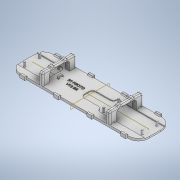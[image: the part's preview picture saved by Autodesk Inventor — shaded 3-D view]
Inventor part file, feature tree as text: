
AUTODESK INVENTOR PART (.ipt)
format: ipt  version: 2021 (Build 250183000, 183)  size: 2,626,048 bytes
history: native  units: in
note: dims shown in document units (in); Inventor stores cm internally (conversion verified against a paired STEP export)
features: sketch x16, extrude x11, fillet x7, mirror x6, revolve x5, plane x2
ambient origin geometry x8: Origin, YZ Plane, XZ Plane, XY Plane, X Axis, Y Axis, Z Axis, Center Point
bodies: Solid1 (feature_tree)
feature tree (47):
  extrude  "Extrusion1"  Depth=4.9606in
  extrude  "Extrusion2"  TaperAngle=0.0deg  [1 undecoded]
  extrude  "Extrusion3"  Depth=0.2362in
  plane  "Work Plane1"
  plane  "Work Plane2"
  extrude  "Extrusion5"  TaperAngle=0.0deg  [1 undecoded]
  fillet  "Fillet2"  [1 undecoded]
  mirror  "Mirror3"
  extrude  "Extrusion6"  TaperAngle=0.0deg  [1 undecoded]
  extrude  "Extrusion7"  TaperAngle=0.0deg  [1 undecoded]
  extrude  "Extrusion9"  TaperAngle=0.0deg  [1 undecoded]
  extrude  "Extrusion10"  Depth=0.2362in
  fillet  "Fillet4"  Radius=1.3386in
  mirror  "Mirror4"
  mirror  "Mirror5"
  fillet  "Fillet5"  [1 undecoded]
  extrude  "Extrusion11"  TaperAngle=0.0deg  [1 undecoded]
  fillet  "Fillet6"  [1 undecoded]
  revolve  "Revolution1"  [1 undecoded]
  revolve  "Revolution2"  [1 undecoded]
  revolve  "Revolution3"  [1 undecoded]
  revolve  "Revolution4"  [1 undecoded]
  extrude  "Extrusion12"  Depth=0.0945in
  revolve  "Revolution5"  [1 undecoded]
  extrude  "Extrusion13"  TaperAngle=0.0deg  [1 undecoded]
  mirror  "Mirror8"
  mirror  "Mirror9"
  mirror  "Mirror10"
  fillet  "Fillet9"  [1 undecoded]
  fillet  "Fillet10"  [1 undecoded]
  fillet  "Fillet11"  Radius=0.7in
  sketch  "Sketch1"  dims[d0=0.1102in d1=0.0in d2=4.9606in]
  sketch  "Sketch2"  dims[d3=1.5512in d4=0.0in]
  sketch  "Sketch3"  dims[d5=0.0in d6=0.2362in]
  sketch  "Sketch6"  dims[d7=0.0787in d8=0.0in d9=0.0in d10=0.0in]
  sketch  "Sketch7"  dims[d11=0.0in d12=0.0in]
  sketch  "Sketch8"  dims[d13=0.0472in d14=0.0in]
  sketch  "Sketch13"  dims[d15=-0.7756in d16=0.0in]
  sketch  "Sketch14"  dims[d17=0.0in d18=0.2362in d19=1.3386in d20=0.0in]
  sketch  "Sketch15"  dims[d21=0.0in d22=0.0in d23=0.0in]
  sketch  "Sketch20"  dims[d24=-2.4803in d28=0.5354in d29=0.0in]
  sketch  "Sketch21"  dims[d30=0.5354in d31=0.9449in]
  sketch  "Sketch22"  dims[d32=2.7559in d33=0.4724in]
  sketch  "Sketch23"  dims[d34=0.7874in d35=0.0394in d36=0.0in]
  sketch  "Sketch25"  dims[d37=0.0945in d38=0.0945in]
  sketch  "Sketch26"  dims[d39=0.0945in d40=0.0945in]
  sketch  "Sketch27"  dims[d41=0.0in d42=0.0in d43=0.0in d44=0.0in d45=0.7in d46=1.8in d47=0.35in d48=0.1811in d49=0.0in d60=1.9685in d61=0.9449in d62=0.4724in d63=1.6929in d64=0.0945in d65=0.0945in d66=0.0945in d67=0.0945in d68=0.0in d69=0.0in d70=0.0in d71=0.0in d72=0.9in d73=0.7in d74=0.35in d75=0.1969in d76=0.5709in d78=0.0in d79=0.4567in d80=0.0in d81=0.0in d82=0.0in d83=0.0in d84=0.0in d85=0.0787in d86=0.0in d88=0.0787in d89=0.1575in d90=0.7874in d91=0.3937in d92=0.0394in d93=0.0in d96=0.9843in d97=0.5512in d98=0.2756in d99=0.1969in d111=90.0deg d112=90.0deg d113=90.0deg d114=90.0deg d116=0.2362in d117=0.0in d118=0.0in d119=0.1181in d120=0.0394in d121=0.0in d122=0.0787in d123=0.0394in d124=180.0deg d125=0.0787in d126=0.1181in d127=0.0157in d128=0.0in d131=0.0394in d132=0.0472in d133=0.0551in]
note: 17 required parameter values undecoded (feature->parameter linkage not recoverable at this tier; creation-order binding heuristic only, values carry confidence <= 0.55)